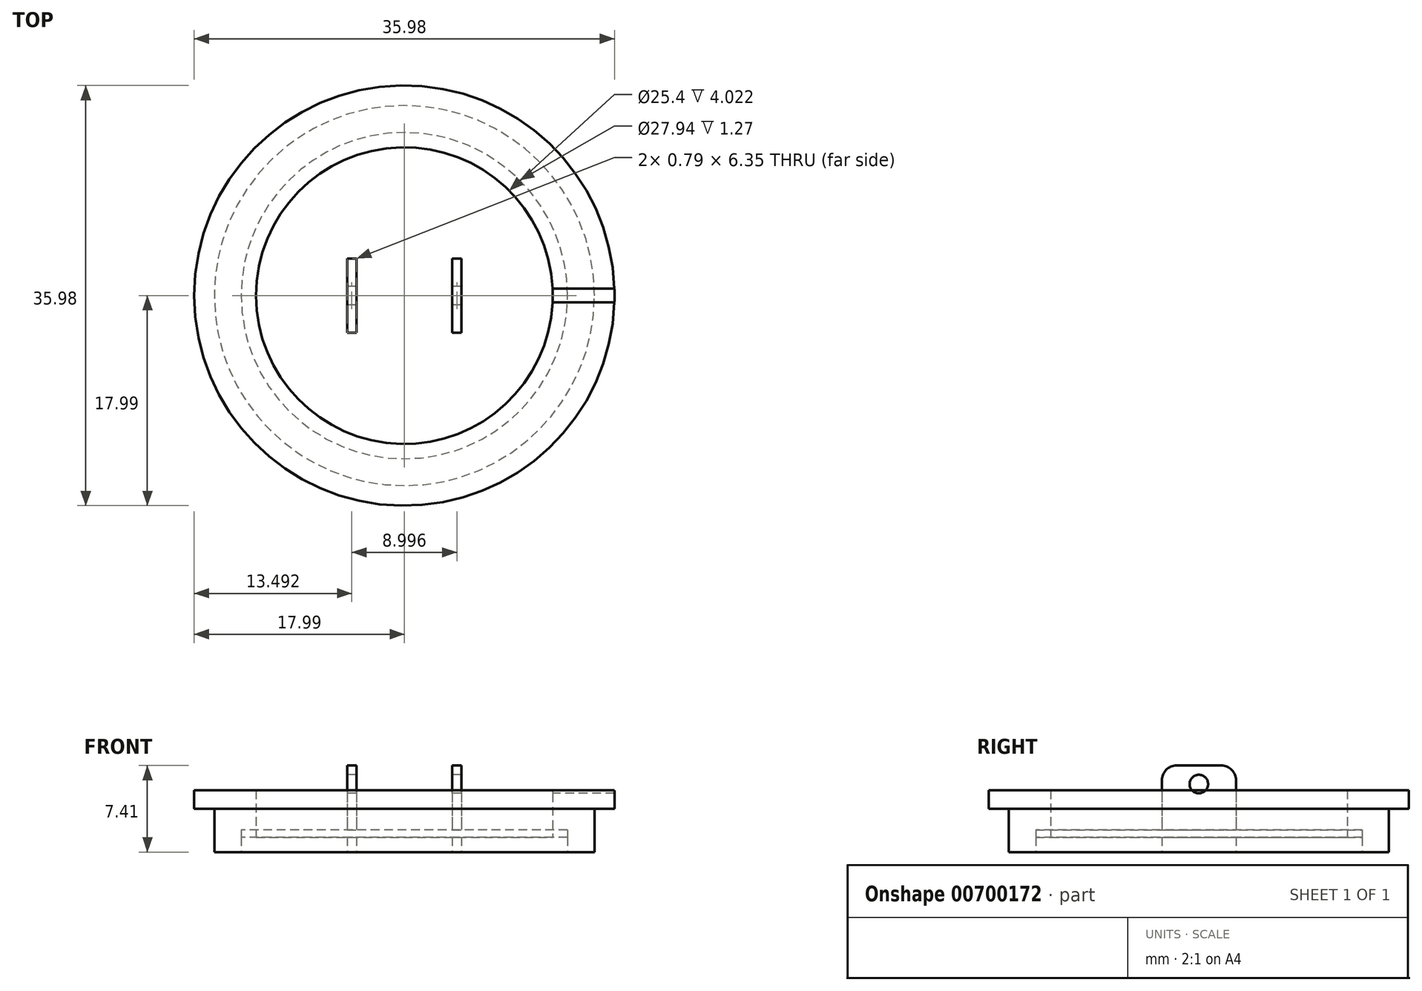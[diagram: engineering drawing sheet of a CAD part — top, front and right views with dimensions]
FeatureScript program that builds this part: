
annotation { "Feature Type Name" : "Feature", "Feature Type Description" : "" }
export const myFeature = defineFeature(function(context is Context, id is Id, definition is map)
    precondition{}
    {
        {
            var Q0;
            Q0=qCreatedBy(makeId("Top.planeOp"),FACE);
            var sketch = newSketch(context, id + "F0", { "sketchPlane" : qUnion([Q0])});
            skCircle(sketch, "E0", {"center": v(0, 0) * mm, "radius": 12.7 * mm});
            skCircle(sketch, "E1", {"center": v(0, 0) * mm, "radius": 16.27 * mm});
            skCircle(sketch, "E2", {"center": v(0, 0) * mm, "radius": 18 * mm});
            skSolve(sketch);
        }
        {
            var Q0;
            Q0=makeQuery(id+"F0.imprint","IMPRINT",FACE,{"disambiguationData":[TD([[makeQuery(id+"F0.imprint","IMPRINT",EDGE,{"derivedFrom":sQuery(id+"F0.wireOp",EDGE,"E0")}),-1.0]])]});
            extrude(context, id + "F1", {"entities" : qUnion([Q0]), "depth" : 5.3 * mm, "offsetDistance" : 25.4 * mm});
        }
        {
            var Q0;
            Q0=makeQuery(id+"F0.imprint","IMPRINT",FACE,{"disambiguationData":[TD([[makeQuery(id+"F0.imprint","IMPRINT",EDGE,{"derivedFrom":sQuery(id+"F0.wireOp",EDGE,"E1")}),-1.0]])]});
            extrude(context, id + "F2", {"entities" : qUnion([Q0]), "operationType" : NewBodyOperationType.ADD, "depth" : 5.3 * mm, "offsetDistance" : 25.4 * mm, "hasSecondDirection" : true, "secondDirectionOppositeDirection" : false, "secondDirectionDepth" : 3.7 * mm});
        }
        {
            var Q0;
            Q0=qCreatedBy(makeId("Top.planeOp"),FACE);
            var sketch = newSketch(context, id + "F3", { "sketchPlane" : qUnion([Q0])});
            skCircle(sketch, "E3", {"center": v(0, 0) * mm, "radius": 13.97 * mm});
            skSolve(sketch);
        }
        {
            var Q0;
            Q0 = qSketchRegion(id + "F3", true);
            extrude(context, id + "F4", {"entities" : qUnion([Q0]), "depth" : 1.9 * mm, "offsetDistance" : 25.4 * mm});
        }
        {
            var Q0;
            Q0 = qSketchRegion(id + "F3", true);
            extrude(context, id + "F5", {"entities" : qUnion([Q0]), "operationType" : NewBodyOperationType.REMOVE, "depth" : 1.27 * mm, "offsetDistance" : 25.4 * mm});
        }
        {
            var Q0;
            Q0=qCreatedBy(makeId("Top.planeOp"),FACE);
            var sketch = newSketch(context, id + "F6", { "sketchPlane" : qUnion([Q0])});
            skLineSegment(sketch, "E4", {"start": v(0, 0) * mm, "end": v(4.5, 0) * mm, "construction": true});
            skLineSegment(sketch, "E5", {"start": v(0, 0) * mm, "end": v(-4.5, 0) * mm, "construction": true});
            skLineSegment(sketch, "E6.bottom", {"start": v(-4.1, 3.17) * mm, "end": v(-4.9, 3.17) * mm});
            skLineSegment(sketch, "E6.top", {"start": v(-4.1, -3.18) * mm, "end": v(-4.9, -3.18) * mm});
            skLineSegment(sketch, "E6.left", {"start": v(-4.1, 3.17) * mm, "end": v(-4.1, -3.18) * mm});
            skLineSegment(sketch, "E6.right", {"start": v(-4.9, 3.17) * mm, "end": v(-4.9, -3.18) * mm});
            skPoint(sketch, "E6.middle", {"position": v(-4.5, 0) * mm});
            skLineSegment(sketch, "E7.bottom", {"start": v(4.9, 3.17) * mm, "end": v(4.1, 3.17) * mm});
            skLineSegment(sketch, "E7.top", {"start": v(4.9, -3.18) * mm, "end": v(4.1, -3.18) * mm});
            skLineSegment(sketch, "E7.left", {"start": v(4.9, 3.18) * mm, "end": v(4.9, -3.18) * mm});
            skLineSegment(sketch, "E7.right", {"start": v(4.1, 3.17) * mm, "end": v(4.1, -3.18) * mm});
            skPoint(sketch, "E7.middle", {"position": v(4.5, 0) * mm});
            skSolve(sketch);
        }
        {
            var Q0;
            Q0 = qSketchRegion(id + "F6", true);
            extrude(context, id + "F7", {"entities" : qUnion([Q0]), "operationType" : NewBodyOperationType.ADD, "depth" : 7.4 * mm, "offsetDistance" : 25.4 * mm});
        }
        {
            var Q0;
            Q0=makeQuery(id+"F7.opExtrude","CAP_EDGE",EDGE,{"disambiguationData":[OSD([sQuery(id+"F6.wireOp",EDGE,"E6.top")])],"isStart":false});
            var Q1;
            Q1=makeQuery(id+"F7.opExtrude","CAP_EDGE",EDGE,{"disambiguationData":[OSD([sQuery(id+"F6.wireOp",EDGE,"E7.top")])],"isStart":false});
            var Q2;
            Q2=makeQuery(id+"F7.opExtrude","CAP_EDGE",EDGE,{"disambiguationData":[OSD([sQuery(id+"F6.wireOp",EDGE,"E7.bottom")])],"isStart":false});
            var Q3;
            Q3=makeQuery(id+"F7.opExtrude","CAP_EDGE",EDGE,{"disambiguationData":[OSD([sQuery(id+"F6.wireOp",EDGE,"E6.bottom")])],"isStart":false});
            fillet(context, id + "F8", {"entities" : qUnion([Q0, Q1, Q2, Q3]), "radius" : 1.27 * mm, "tangentPropagation" : true, "allowEdgeOverflow" : false});
        }
        {
            var Q0;
            Q0=makeQuery(id+"F7.opExtrude","SWEPT_FACE",FACE,{"disambiguationData":[OSD([sQuery(id+"F6.wireOp",EDGE,"E6.right")])]});
            var sketch = newSketch(context, id + "F9", { "sketchPlane" : qUnion([Q0])});
            skLineSegment(sketch, "E8", {"start": v(0, 7.4) * mm, "end": v(0, 5.82) * mm, "construction": true});
            skCircle(sketch, "E9", {"center": v(0, 5.82) * mm, "radius": 0.8 * mm});
            skSolve(sketch);
        }
        {
            var Q0;
            Q0 = qSketchRegion(id + "F9", true);
            extrude(context, id + "F10", {"entities" : qUnion([Q0]), "operationType" : NewBodyOperationType.REMOVE, "oppositeDirection" : true, "depth" : 25.4 * mm, "offsetDistance" : 25.4 * mm});
        }
    });
